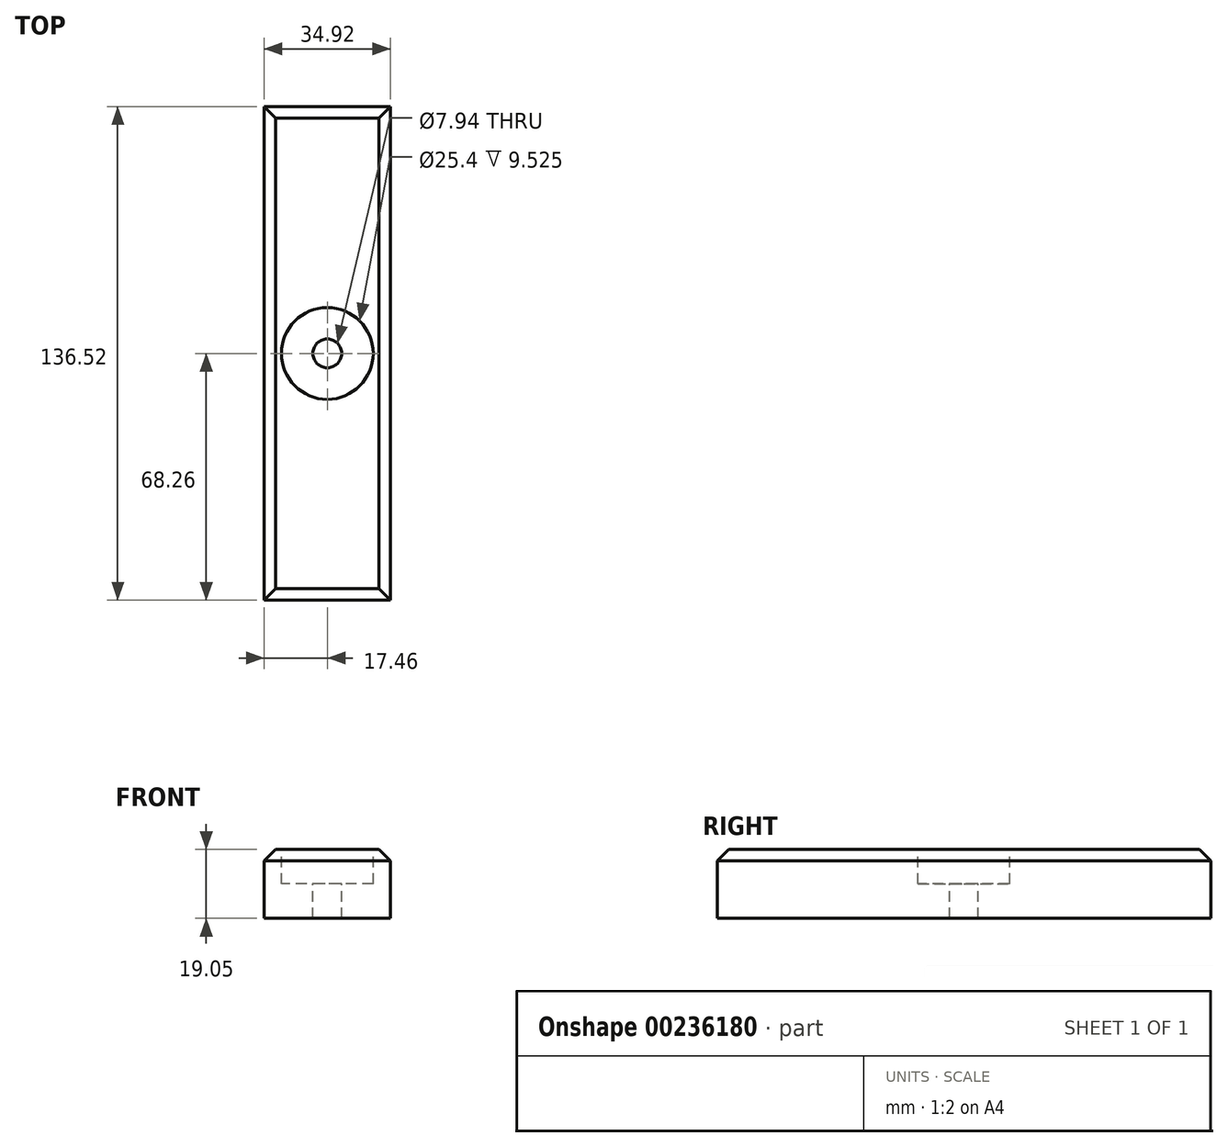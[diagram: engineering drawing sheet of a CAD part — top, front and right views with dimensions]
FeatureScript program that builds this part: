
annotation { "Feature Type Name" : "Feature", "Feature Type Description" : "" }
export const myFeature = defineFeature(function(context is Context, id is Id, definition is map)
    precondition{}
    {
        {
            var Q0;
            Q0=qCreatedBy(makeId("Top.planeOp"),FACE);
            var sketch = newSketch(context, id + "F0", { "sketchPlane" : qUnion([Q0])});
            skLineSegment(sketch, "E0.bottom", {"start": v(-17.46, 68.26) * mm, "end": v(17.46, 68.26) * mm});
            skLineSegment(sketch, "E0.top", {"start": v(-17.46, -68.26) * mm, "end": v(17.46, -68.26) * mm});
            skLineSegment(sketch, "E0.left", {"start": v(-17.46, 68.26) * mm, "end": v(-17.46, -68.26) * mm});
            skLineSegment(sketch, "E0.right", {"start": v(17.46, 68.26) * mm, "end": v(17.46, -68.26) * mm});
            skPoint(sketch, "E0.middle", {"position": v(0, 0) * mm});
            skSolve(sketch);
        }
        {
            var Q0;
            Q0=makeQuery(id+"F0.imprint","IMPRINT",FACE,{"disambiguationData":[TD([[makeQuery(id+"F0.imprint","IMPRINT",EDGE,{"derivedFrom":sQuery(id+"F0.wireOp",EDGE,"E0.bottom")}),-1.0]])]});
            extrude(context, id + "F1", {"entities" : qUnion([Q0]), "oppositeDirection" : true, "depth" : 19.05 * mm});
        }
        {
            var Q0;
            Q0=makeQuery(id+"F1.opExtrude","CAP_FACE",FACE,{"disambiguationData":[OSD([sQuery(id+"F0.wireOp",EDGE,"E0.bottom"),sQuery(id+"F0.wireOp",EDGE,"E0.top"),sQuery(id+"F0.wireOp",EDGE,"E0.left"),sQuery(id+"F0.wireOp",EDGE,"E0.right")])],"isStart":true});
            chamfer(context, id + "F2", {"entities" : qUnion([Q0]), "chamferType" : ChamferType.OFFSET_ANGLE, "width" : 3.17 * mm, "oppositeDirection" : false, "angle" : 45 * degree, "tangentPropagation" : true});
        }
        {
            var Q0;
            Q0=qCreatedBy(makeId("Top.planeOp"),FACE);
            var sketch = newSketch(context, id + "F3", { "sketchPlane" : qUnion([Q0])});
            skCircle(sketch, "E1", {"center": v(0, 0) * mm, "radius": 3.97 * mm});
            skSolve(sketch);
        }
        {
            var Q0;
            Q0=sQuery(id+"F3.wireOp",VERTEX,"E1.center");
            var Q1;
            Q1=makeQuery(id+"F1.opExtrude","SWEPT_BODY",BODY,{"disambiguationData":[OSD([sQuery(id+"F0.wireOp",EDGE,"E0.bottom"),sQuery(id+"F0.wireOp",EDGE,"E0.top"),sQuery(id+"F0.wireOp",EDGE,"E0.left"),sQuery(id+"F0.wireOp",EDGE,"E0.right")])]});
            hole(context, id + "F4", {"style" : HoleStyle.C_BORE, "endStyle" : HoleEndStyle.THROUGH, "holeDiameter" : 7.94 * mm, "cBoreDiameter" : 25.4 * mm, "cBoreDepth" : 9.52 * mm, "locations" : qUnion([Q0]), "scope" : qUnion([Q1]), "isTappedThrough" : true});
        }
    });
